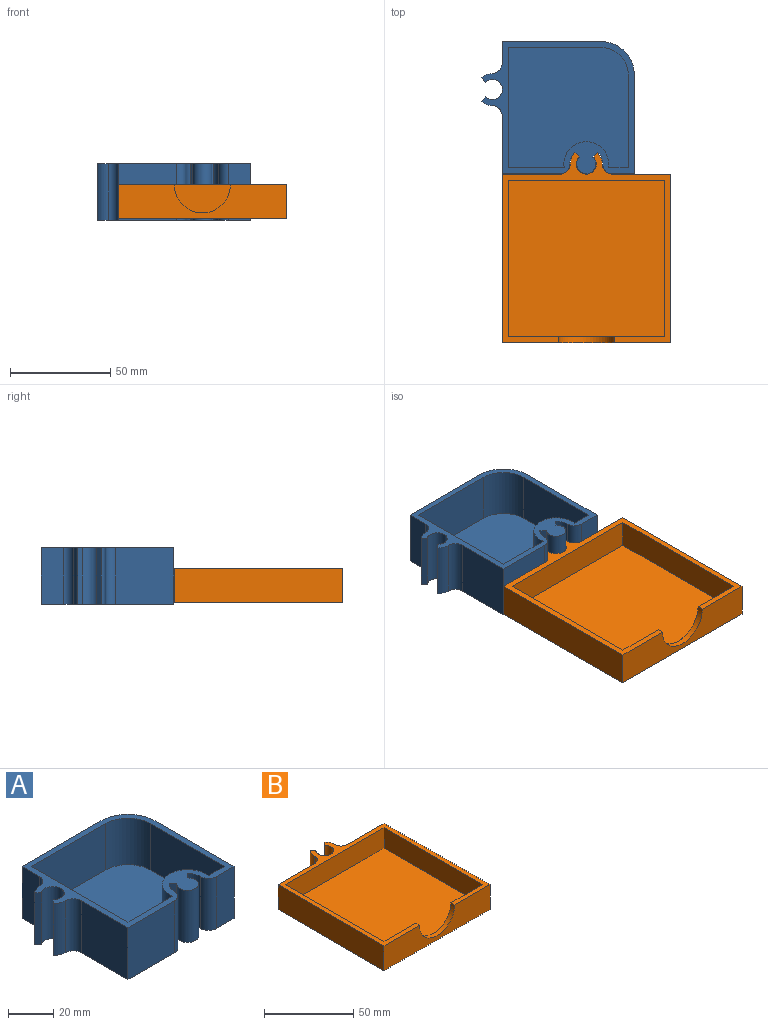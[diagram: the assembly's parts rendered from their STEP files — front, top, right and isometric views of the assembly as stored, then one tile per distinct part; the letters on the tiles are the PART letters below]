
ASSEMBLY  parts=2 mates=1
PART A: 31 faces, bbox 76.3x66x28 mm
  f0: plane 29x28mm, normal (-1,0,0), area 812mm2, adj f12,f14,f15,f28
  f1: cylinder r=8.2mm len=28mm, axis (0,0,-1), area 185.9mm2, adj f2,f13,f14,f15
  f2: plane 28x2.41mm, normal (-0.71,-0.71,0), area 95.2mm2, adj f1,f3,f14,f15
  f3: cylinder r=4.8mm len=28mm, axis (0,0,-1), area 644.5mm2, adj f2,f4,f14,f15
  f4: plane 28x2.41mm, normal (0.71,-0.71,0), area 95.2mm2, adj f3,f5,f14,f15
  f5: cylinder r=8.2mm len=28mm, axis (0,0,-1), area 185.9mm2, adj f4,f6,f14,f15
  f6: cylinder r=4.8mm len=28mm, axis (0,0,-1), area 211.1mm2, adj f5,f7,f14,f15
  f7: plane 28x11mm, normal (0,-1,0), area 308mm2, adj f6,f8,f14,f15
  f8: plane 49.17x28mm, normal (1,0,0), area 1376.7mm2, adj f7,f9,f14,f15
  f9: cylinder r=16.83mm len=28mm, axis (0,0,-1), area 740.3mm2, adj f8,f10,f14,f15
  f10: plane 49.17x28mm, normal (0,1,0), area 1376.7mm2, adj f9,f11,f14,f15
  f11: plane 28x11mm, normal (-1,0,0), area 308mm2, adj f10,f14,f15,f26
  f12: plane 29x28mm, normal (0,-1,0), area 812mm2, adj f0,f13,f14,f15
  f13: cylinder r=4.8mm len=28mm, axis (0,0,-1), area 211.1mm2, adj f1,f12,f14,f15
  f14: plane 76.28x66mm, normal (0,0,-1), area 4284.1mm2, adj f0,f1,f2,f3,f4,f5,f6,f7
  f15: plane 76.28x66mm, normal (0,0,1), area 962.3mm2, adj f0,f1,f2,f3,f4,f5,f6,f7
  f16: plane 46.17x25mm, normal (-1,0,0), area 1154.2mm2, adj f15,f17,f22,f23
  f17: cylinder r=13.83mm len=25mm, axis (0,0,-1), area 543.2mm2, adj f15,f16,f18,f23
  f18: plane 46.17x25mm, normal (0,-1,0), area 1154.2mm2, adj f15,f17,f19,f23
  f19: plane 60x25mm, normal (1,0,0), area 1500mm2, adj f15,f18,f20,f23
  f20: plane 27.95x25mm, normal (0,1,0), area 698.6mm2, adj f15,f19,f21,f23
  f21: cylinder r=11.2mm len=25mm, axis (0,0,-1), area 970mm2, adj f15,f20,f22,f23
  f22: plane 25x9.95mm, normal (0,1,0), area 248.6mm2, adj f15,f16,f21,f23
  f23: plane 60x60mm, normal (0,0,1), area 3321.8mm2, adj f16,f17,f18,f19,f20,f21,f22
  f24: plane 28x2.12mm, normal (-0.71,-0.71,0), area 84.1mm2, adj f14,f15,f25,f27
  f25: cylinder r=5mm len=28mm, axis (0,0,-1), area 645.7mm2, adj f14,f15,f24,f29
  f26: cylinder r=5mm len=28mm, axis (0,0,-1), area 217.8mm2, adj f11,f14,f15,f27
  f27: cylinder r=8mm len=28mm, axis (0,0,-1), area 165.5mm2, adj f14,f15,f24,f26
  f28: cylinder r=5mm len=28mm, axis (0,0,-1), area 217.8mm2, adj f0,f14,f15,f30
  f29: plane 28x2.12mm, normal (-0.71,0.71,0), area 84.1mm2, adj f14,f15,f25,f30
  f30: cylinder r=8mm len=28mm, axis (0,0,-1), area 165.5mm2, adj f14,f15,f28,f29
PART B: 21 faces, bbox 84x94.7x17 mm
  f0: plane 39x14mm, normal (0,1,0), area 392.1mm2, adj f5,f18,f19,f20
  f1: plane 39x14mm, normal (0,1,0), area 392.1mm2, adj f6,f18,f19,f20
  f2: plane 84x17mm, normal (0,-1,0), area 1120.1mm2, adj f3,f7,f8,f18,f20
  f3: plane 94.66x84mm, normal (0,0,-1), area 7138.1mm2, adj f2,f7,f8,f9,f10,f11,f12,f13
  f4: plane 78x14mm, normal (0,-1,0), area 1092mm2, adj f5,f6,f18,f19
  f5: plane 78x14mm, normal (1,0,0), area 1092mm2, adj f0,f4,f18,f19
  f6: plane 78x14mm, normal (-1,0,0), area 1092mm2, adj f1,f4,f18,f19
  f7: plane 84x17mm, normal (-1,0,0), area 1428mm2, adj f2,f3,f17,f18
  f8: plane 84x17mm, normal (1,0,0), area 1428mm2, adj f2,f3,f9,f18
  f9: plane 29x17mm, normal (0,1,0), area 493mm2, adj f3,f8,f10,f18
  f10: cylinder r=5mm len=17mm, axis (0,0,-1), area 133.5mm2, adj f3,f9,f11,f18
  f11: cylinder r=8mm len=17mm, axis (0,0,-1), area 106.8mm2, adj f3,f10,f12,f18
  f12: plane 17x2.12mm, normal (-0.71,0.71,0), area 51mm2, adj f3,f11,f13,f18
  f13: cylinder r=5mm len=17mm, axis (0,0,-1), area 400.6mm2, adj f3,f12,f14,f18
  f14: plane 17x2.12mm, normal (0.71,0.71,0), area 51mm2, adj f3,f13,f15,f18
  f15: cylinder r=8mm len=17mm, axis (0,0,-1), area 106.8mm2, adj f3,f14,f16,f18
  f16: cylinder r=5mm len=17mm, axis (0,0,-1), area 133.5mm2, adj f3,f15,f17,f18
  f17: plane 29x17mm, normal (0,1,0), area 493mm2, adj f3,f7,f16,f18
  f18: plane 94.66x84mm, normal (0,0,1), area 970.1mm2, adj f0,f1,f2,f4,f5,f6,f7,f8
  f19: plane 78x78mm, normal (0,0,1), area 6084mm2, adj f0,f1,f4,f5,f6
  f20: cylinder r=14mm len=28mm, axis (0,-1,0), area 131.9mm2, adj f0,f1,f2,f18
PLACE A t=(-33.1,12.2,-12.89)mm
PLACE B t=(-33.1,12.2,-12.31)mm
MATE slider A.f1 <-> B.f11  axis (0,0,-1) through (8.9,17.2,-12.89)mm
